# Revit family: AFX_Inc-Watson-Wall_Sconce
name_source: partatom
category: Lighting Fixtures
revit_build: Autodesk Revit 2016 (Build: 20150220_1215(x64)
units: mm (PartAtom-declared; Revit-internal decimal feet)

## family parameters
Cut with Voids When Loaded = No
Host = Face
Light Source = Yes
Part Type = Normal
Room Calculation Point = No
Round Connector Dimension = Use Diameter
Shared = No

## types (2) — shared parameters
Assembly Code = E1020300
CRI = 90
Color Filter = 16777215
Default Elevation = 48"
Description = 6'' LED Outdoor Wall Sconce Black
Dimming Lamp Color Temperature Shift = <None>
Emit Shape Visible in Rendering = No
Emit from Rectangle Length = 4 21/32"
Emit from Rectangle Width = 2 19/32"
Height = 5 31/32"
Keynote = 12500
Length = 3 1/2"
Manufacturer = AFX Inc
Model = WTNW0506L30D2BK
Photometric Web File = WTNW0506L30D2xx_IES.IES
Screen Finish = AFX - Diffuser Frosted
Tilt Angle = 90.00°
Type Comments = Watson
URL = www.afxinc.com
Voltage = 120 V
Wattage Comments = 12W
Width = 5"

## per-type parameters (varying)
| type | Body Finish | Support Finish |
| WTNW0506L30D2BK | AFX - Metal Powder Coated Black | AFX - Metal Powder Coated Black |
| WTNW0506L30D2WH | AFX - Metal Powder Coated White | AFX - Metal Powder Coated White |

## geometry (parser evidence)
native form markers: Sweep x1
no freeform markers — native parametric forms only
